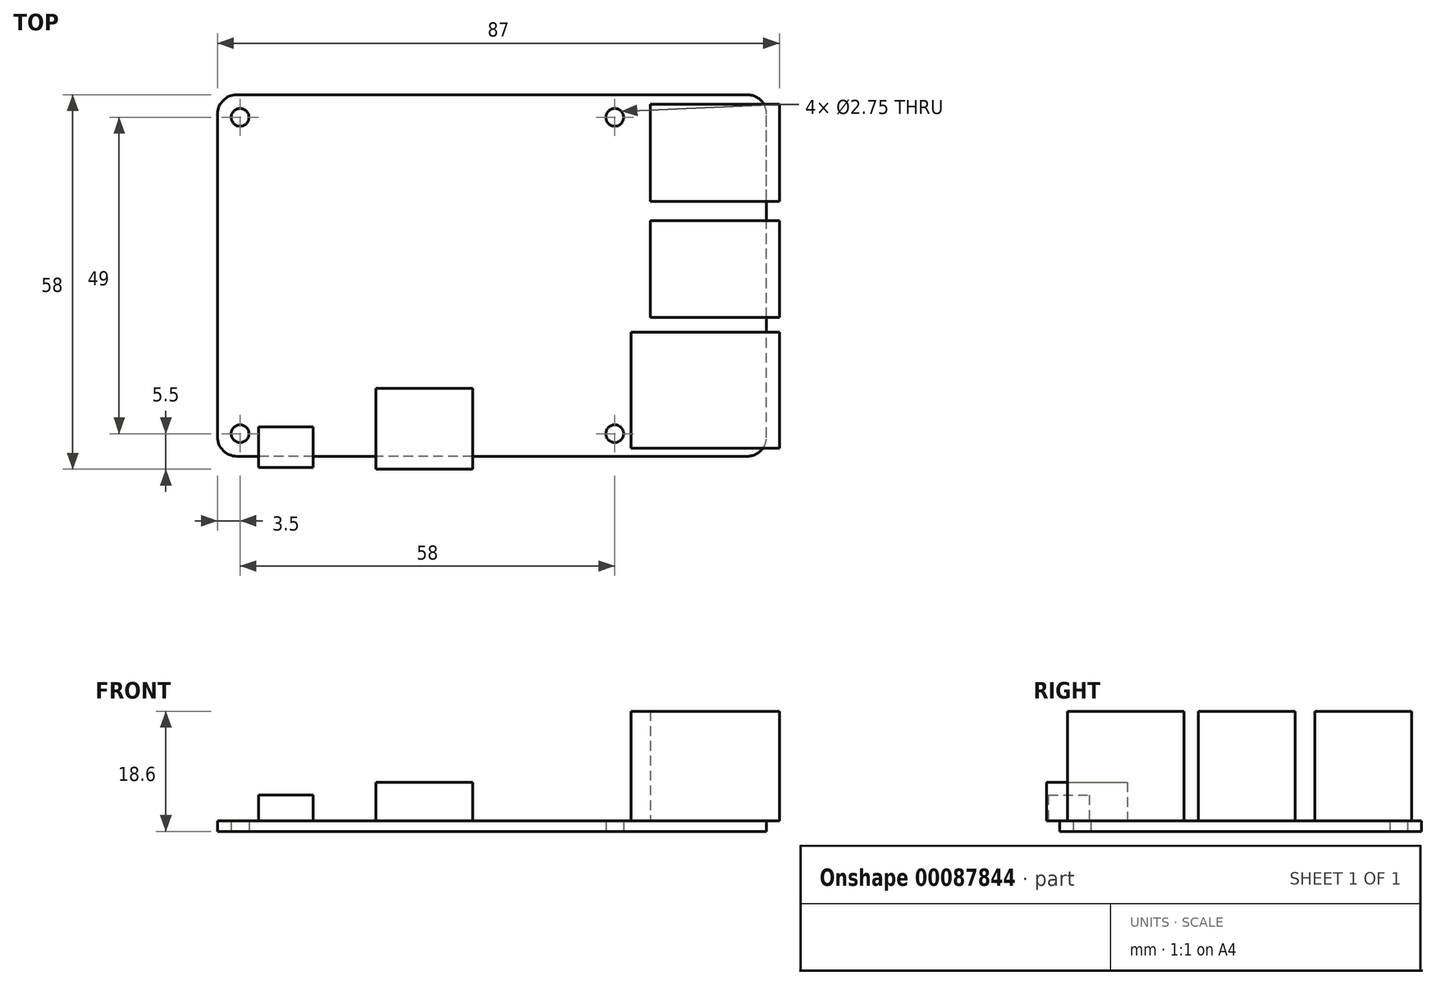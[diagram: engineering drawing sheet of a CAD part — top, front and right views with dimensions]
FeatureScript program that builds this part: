
annotation { "Feature Type Name" : "Feature", "Feature Type Description" : "" }
export const myFeature = defineFeature(function(context is Context, id is Id, definition is map)
    precondition{}
    {
        {
            var Q0;
            Q0=qCreatedBy(makeId("Top.planeOp"),FACE);
            var sketch = newSketch(context, id + "F0", { "sketchPlane" : qUnion([Q0])});
            skLineSegment(sketch, "E0.bottom", {"start": v(39.5, -28) * mm, "end": v(-39.5, -28) * mm});
            skLineSegment(sketch, "E0.top", {"start": v(39.5, 28) * mm, "end": v(-39.5, 28) * mm});
            skLineSegment(sketch, "E0.left", {"start": v(42.5, -25) * mm, "end": v(42.5, 25) * mm});
            skLineSegment(sketch, "E0.right", {"start": v(-42.5, -25) * mm, "end": v(-42.5, 25) * mm});
            skPoint(sketch, "E0.middle", {"position": v(0, 0) * mm});
            skPoint(sketch, "E1.visualSharp", {"position": v(-42.5, 28) * mm});
            skArc(sketch, "E1.filletArc", {"start": v(-39.5, 28) * mm, "mid": v(-41.62, 27.12) * mm, "end": v(-42.5, 25) * mm});
            skPoint(sketch, "E2.visualSharp", {"position": v(42.5, 28) * mm});
            skArc(sketch, "E2.filletArc", {"start": v(42.5, 25) * mm, "mid": v(41.62, 27.12) * mm, "end": v(39.5, 28) * mm});
            skPoint(sketch, "E3.visualSharp", {"position": v(-42.5, -28) * mm});
            skArc(sketch, "E3.filletArc", {"start": v(-42.5, -25) * mm, "mid": v(-41.62, -27.12) * mm, "end": v(-39.5, -28) * mm});
            skPoint(sketch, "E4.visualSharp", {"position": v(42.5, -28) * mm});
            skArc(sketch, "E4.filletArc", {"start": v(39.5, -28) * mm, "mid": v(41.62, -27.12) * mm, "end": v(42.5, -25) * mm});
            skCircle(sketch, "E5", {"center": v(-39, 24.5) * mm, "radius": 1.38 * mm});
            skCircle(sketch, "E6", {"center": v(19, 24.5) * mm, "radius": 1.38 * mm});
            skCircle(sketch, "E7", {"center": v(-39, -24.5) * mm, "radius": 1.38 * mm});
            skCircle(sketch, "E8", {"center": v(19, -24.5) * mm, "radius": 1.38 * mm});
            skSolve(sketch);
        }
        {
            var Q0;
            Q0=makeQuery(id+"F0.imprint","IMPRINT",FACE,{"disambiguationData":[TD([[makeQuery(id+"F0.imprint","IMPRINT",EDGE,{"derivedFrom":sQuery(id+"F0.wireOp",EDGE,"E0.bottom")}),-1.0]])]});
            extrude(context, id + "F1", {"entities" : qUnion([Q0]), "depth" : 1.6 * mm});
        }
        {
            var Q0;
            Q0=makeQuery(id+"F1.opExtrude","CAP_FACE",FACE,{"disambiguationData":[OSD([sQuery(id+"F0.wireOp",EDGE,"E0.bottom"),sQuery(id+"F0.wireOp",EDGE,"E0.top"),sQuery(id+"F0.wireOp",EDGE,"E0.left"),sQuery(id+"F0.wireOp",EDGE,"E0.right"),sQuery(id+"F0.wireOp",EDGE,"E1.filletArc"),sQuery(id+"F0.wireOp",EDGE,"E2.filletArc"),sQuery(id+"F0.wireOp",EDGE,"E3.filletArc"),sQuery(id+"F0.wireOp",EDGE,"E4.filletArc"),sQuery(id+"F0.wireOp",EDGE,"E5"),sQuery(id+"F0.wireOp",EDGE,"E6"),sQuery(id+"F0.wireOp",EDGE,"E7"),sQuery(id+"F0.wireOp",EDGE,"E8")])],"isStart":false});
            var sketch = newSketch(context, id + "F2", { "sketchPlane" : qUnion([Q0])});
            skLineSegment(sketch, "E9.bottom", {"start": v(-27.67, -29.74) * mm, "end": v(-36.13, -29.74) * mm});
            skLineSegment(sketch, "E9.top", {"start": v(-27.67, -23.43) * mm, "end": v(-36.13, -23.43) * mm});
            skLineSegment(sketch, "E9.left", {"start": v(-27.67, -29.74) * mm, "end": v(-27.67, -23.43) * mm});
            skLineSegment(sketch, "E9.right", {"start": v(-36.13, -29.74) * mm, "end": v(-36.13, -23.43) * mm});
            skPoint(sketch, "E9.middle", {"position": v(-31.9, -26.59) * mm});
            skSolve(sketch);
        }
        {
            var Q0;
            {var subQ0=sQuery(id+"F2.wireOp",EDGE,"E9.bottom");Q0=makeQuery(id+"F2.imprint","IMPRINT",FACE,{"disambiguationData":[TD([[makeQuery(id+"F2.imprint","IMPRINT",EDGE,{"derivedFrom":subQ0}),-1.0]])]});}
            var Q1;
            {var subQ0=sQuery(id+"F2.wireOp",EDGE,"E9.top");Q1=makeQuery(id+"F2.imprint","IMPRINT",FACE,{"disambiguationData":[TD([[makeQuery(id+"F2.imprint","IMPRINT",EDGE,{"derivedFrom":subQ0}),1.0]])]});}
            extrude(context, id + "F3", {"entities" : qUnion([Q0, Q1]), "operationType" : NewBodyOperationType.ADD, "depth" : 4 * mm});
        }
        {
            var Q0;
            Q0=makeQuery(id+"F1.opExtrude","CAP_FACE",FACE,{"disambiguationData":[OSD([sQuery(id+"F0.wireOp",EDGE,"E0.bottom"),sQuery(id+"F0.wireOp",EDGE,"E0.top"),sQuery(id+"F0.wireOp",EDGE,"E0.left"),sQuery(id+"F0.wireOp",EDGE,"E0.right"),sQuery(id+"F0.wireOp",EDGE,"E1.filletArc"),sQuery(id+"F0.wireOp",EDGE,"E2.filletArc"),sQuery(id+"F0.wireOp",EDGE,"E3.filletArc"),sQuery(id+"F0.wireOp",EDGE,"E4.filletArc"),sQuery(id+"F0.wireOp",EDGE,"E5"),sQuery(id+"F0.wireOp",EDGE,"E6"),sQuery(id+"F0.wireOp",EDGE,"E7"),sQuery(id+"F0.wireOp",EDGE,"E8")])],"isStart":false});
            var sketch = newSketch(context, id + "F4", { "sketchPlane" : qUnion([Q0])});
            skLineSegment(sketch, "E10.bottom", {"start": v(44.5, 11.5) * mm, "end": v(24.5, 11.5) * mm});
            skLineSegment(sketch, "E10.top", {"start": v(44.5, 26.5) * mm, "end": v(24.5, 26.5) * mm});
            skLineSegment(sketch, "E10.left", {"start": v(44.5, 11.5) * mm, "end": v(44.5, 26.5) * mm});
            skLineSegment(sketch, "E10.right", {"start": v(24.5, 11.5) * mm, "end": v(24.5, 26.5) * mm});
            skPoint(sketch, "E10.middle", {"position": v(34.5, 19) * mm});
            skLineSegment(sketch, "E11.bottom", {"start": v(44.5, -6.5) * mm, "end": v(24.5, -6.5) * mm});
            skLineSegment(sketch, "E11.top", {"start": v(44.5, 8.5) * mm, "end": v(24.5, 8.5) * mm});
            skLineSegment(sketch, "E11.left", {"start": v(44.5, -6.5) * mm, "end": v(44.5, 8.5) * mm});
            skLineSegment(sketch, "E11.right", {"start": v(24.5, -6.5) * mm, "end": v(24.5, 8.5) * mm});
            skPoint(sketch, "E11.middle", {"position": v(34.5, 1) * mm});
            skLineSegment(sketch, "E12.bottom", {"start": v(44.5, -26.75) * mm, "end": v(21.5, -26.75) * mm});
            skLineSegment(sketch, "E12.top", {"start": v(44.5, -8.75) * mm, "end": v(21.5, -8.75) * mm});
            skLineSegment(sketch, "E12.left", {"start": v(44.5, -26.75) * mm, "end": v(44.5, -8.75) * mm});
            skLineSegment(sketch, "E12.right", {"start": v(21.5, -26.75) * mm, "end": v(21.5, -8.75) * mm});
            skPoint(sketch, "E12.middle", {"position": v(33, -17.75) * mm});
            skSolve(sketch);
        }
        {
            var Q0;
            Q0 = qSketchRegion(id + "F4", true);
            extrude(context, id + "F5", {"entities" : qUnion([Q0]), "operationType" : NewBodyOperationType.ADD, "depth" : 17 * mm});
        }
        {
            var Q0;
            Q0=makeQuery(id+"F1.opExtrude","CAP_FACE",FACE,{"disambiguationData":[OSD([sQuery(id+"F0.wireOp",EDGE,"E0.bottom"),sQuery(id+"F0.wireOp",EDGE,"E0.top"),sQuery(id+"F0.wireOp",EDGE,"E0.left"),sQuery(id+"F0.wireOp",EDGE,"E0.right"),sQuery(id+"F0.wireOp",EDGE,"E1.filletArc"),sQuery(id+"F0.wireOp",EDGE,"E2.filletArc"),sQuery(id+"F0.wireOp",EDGE,"E3.filletArc"),sQuery(id+"F0.wireOp",EDGE,"E4.filletArc"),sQuery(id+"F0.wireOp",EDGE,"E5"),sQuery(id+"F0.wireOp",EDGE,"E6"),sQuery(id+"F0.wireOp",EDGE,"E7"),sQuery(id+"F0.wireOp",EDGE,"E8")])],"isStart":false});
            var sketch = newSketch(context, id + "F6", { "sketchPlane" : qUnion([Q0])});
            skLineSegment(sketch, "E13.bottom", {"start": v(-3, -30) * mm, "end": v(-18, -30) * mm});
            skLineSegment(sketch, "E13.top", {"start": v(-3, -17.5) * mm, "end": v(-18, -17.5) * mm});
            skLineSegment(sketch, "E13.left", {"start": v(-3, -30) * mm, "end": v(-3, -17.5) * mm});
            skLineSegment(sketch, "E13.right", {"start": v(-18, -30) * mm, "end": v(-18, -17.5) * mm});
            skPoint(sketch, "E13.middle", {"position": v(-10.5, -23.75) * mm});
            skSolve(sketch);
        }
        {
            var Q0;
            Q0 = qSketchRegion(id + "F6", true);
            extrude(context, id + "F7", {"entities" : qUnion([Q0]), "operationType" : NewBodyOperationType.ADD, "depth" : 6 * mm});
        }
    });
